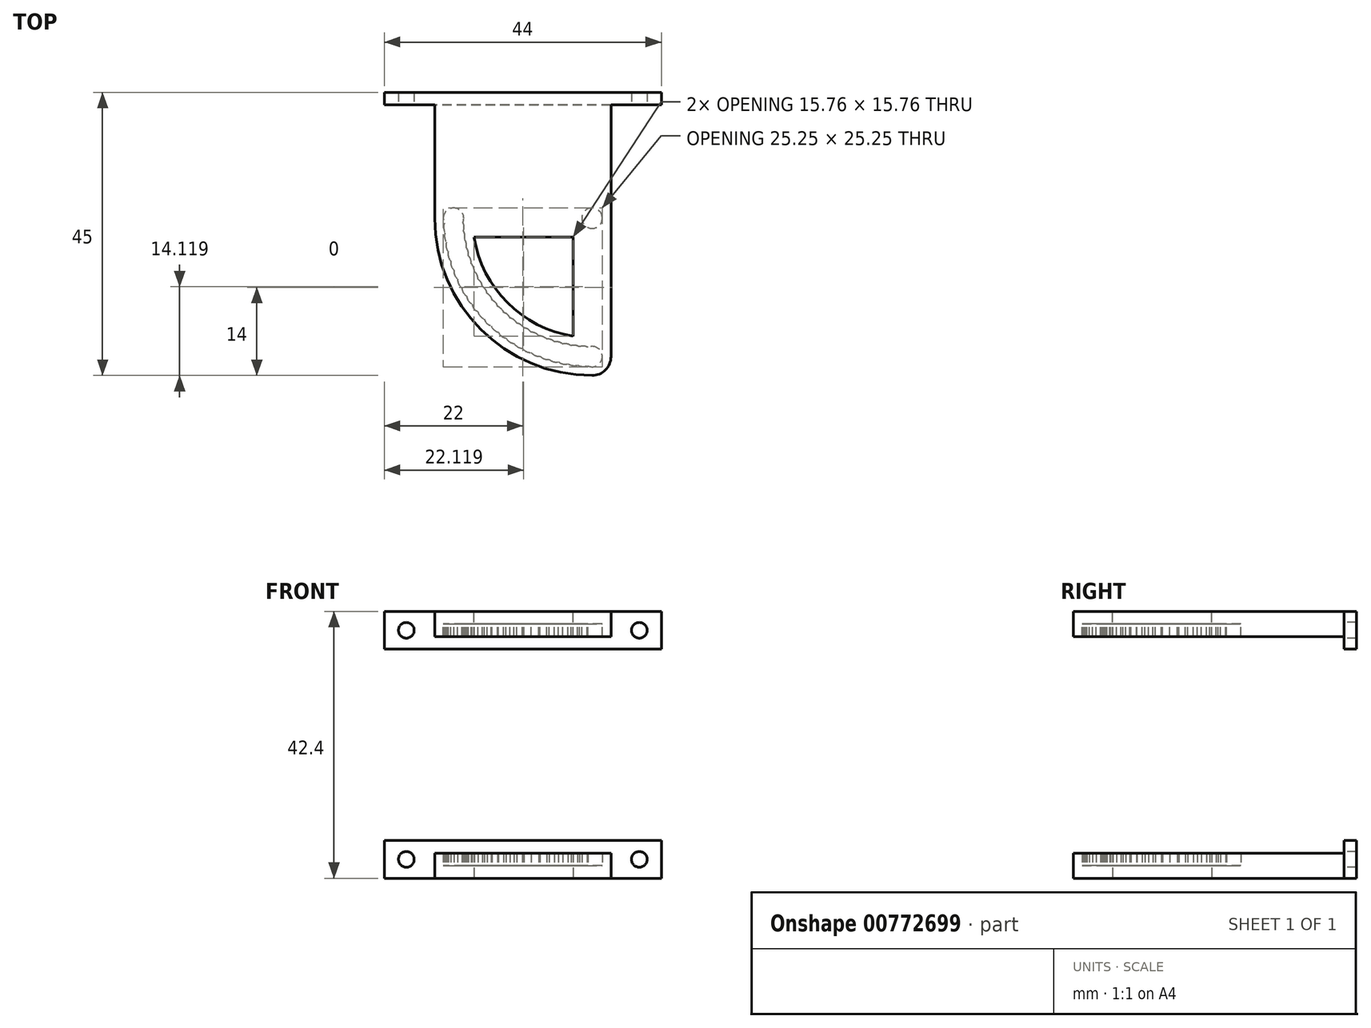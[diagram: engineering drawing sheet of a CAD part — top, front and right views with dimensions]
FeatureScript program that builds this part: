
annotation { "Feature Type Name" : "Feature", "Feature Type Description" : "" }
export const myFeature = defineFeature(function(context is Context, id is Id, definition is map)
    precondition{}
    {
        {
            var Q0;
            Q0=qCreatedBy(makeId("Top.planeOp"),FACE);
            var sketch = newSketch(context, id + "F0", { "sketchPlane" : qUnion([Q0])});
            skArc(sketch, "E0", {"start": v(-25, 0) * mm, "mid": v(-17.68, -17.68) * mm, "end": v(0, -25) * mm});
            skCircle(sketch, "E1", {"center": v(0, 0) * mm, "radius": 1.63 * mm});
            skArc(sketch, "E2", {"start": v(-0.77, -23.43) * mm, "mid": v(1.62, -22.05) * mm, "end": v(-0.67, -20.52) * mm});
            skCircle(sketch, "E3", {"center": v(0, 0) * mm, "radius": 22 * mm, "construction": true});
            skArc(sketch, "E4", {"start": v(-18.76, -3) * mm, "mid": v(-13.44, -13.44) * mm, "end": v(-3, -18.76) * mm});
            skLineSegment(sketch, "E5", {"start": v(3, -22) * mm, "end": v(3, 20) * mm});
            skLineSegment(sketch, "E6", {"start": v(3, 20) * mm, "end": v(-25, 20) * mm});
            skLineSegment(sketch, "E7", {"start": v(-5.92, -22) * mm, "end": v(6.06, -22) * mm, "construction": true});
            skLineSegment(sketch, "E8", {"start": v(-28.17, 0) * mm, "end": v(-21.36, 0) * mm, "construction": true});
            skLineSegment(sketch, "E9", {"start": v(-25, 0) * mm, "end": v(-25, 20) * mm});
            skLineSegment(sketch, "E10", {"start": v(-3, -18.76) * mm, "end": v(-3, -3) * mm});
            skLineSegment(sketch, "E11", {"start": v(-3, -3) * mm, "end": v(-18.76, -3) * mm});
            skArc(sketch, "E12.1.0", {"start": v(-2.3, -23.33) * mm, "mid": v(-1.55, -23.57) * mm, "end": v(-0.77, -23.43) * mm});
            skArc(sketch, "E12.2.0", {"start": v(-3.82, -23.13) * mm, "mid": v(-3.08, -23.42) * mm, "end": v(-2.3, -23.33) * mm});
            skArc(sketch, "E12.3.0", {"start": v(-5.88, -21.93) * mm, "mid": v(-5.87, -21.97) * mm, "end": v(-5.86, -22) * mm});
            skArc(sketch, "E12.4.0", {"start": v(-6.8, -22.44) * mm, "mid": v(-6.11, -22.82) * mm, "end": v(-5.32, -22.83) * mm});
            skArc(sketch, "E12.5.0", {"start": v(-8.26, -21.94) * mm, "mid": v(-7.6, -22.37) * mm, "end": v(-6.8, -22.44) * mm});
            skArc(sketch, "E12.6.0", {"start": v(-9.68, -21.36) * mm, "mid": v(-9.04, -21.83) * mm, "end": v(-8.26, -21.94) * mm});
            skArc(sketch, "E12.7.0", {"start": v(-11.05, -20.68) * mm, "mid": v(-10.45, -21.19) * mm, "end": v(-9.68, -21.36) * mm});
            skArc(sketch, "E12.8.0", {"start": v(-12.38, -19.9) * mm, "mid": v(-11.81, -20.46) * mm, "end": v(-11.05, -20.68) * mm});
            skArc(sketch, "E12.9.0", {"start": v(-13.66, -19.06) * mm, "mid": v(-13.13, -19.64) * mm, "end": v(-12.38, -19.9) * mm});
            skArc(sketch, "E12.10.0", {"start": v(-14.87, -18.12) * mm, "mid": v(-14.38, -18.74) * mm, "end": v(-13.66, -19.06) * mm});
            skArc(sketch, "E12.11.0", {"start": v(-16.03, -17.11) * mm, "mid": v(-15.58, -17.76) * mm, "end": v(-14.87, -18.12) * mm});
            skArc(sketch, "E12.12.0", {"start": v(-17.11, -16.03) * mm, "mid": v(-16.7, -16.7) * mm, "end": v(-16.03, -17.11) * mm});
            skArc(sketch, "E12.13.0", {"start": v(-18.12, -14.87) * mm, "mid": v(-17.76, -15.58) * mm, "end": v(-17.11, -16.03) * mm});
            skArc(sketch, "E12.14.0", {"start": v(-19.06, -13.66) * mm, "mid": v(-18.74, -14.38) * mm, "end": v(-18.12, -14.87) * mm});
            skArc(sketch, "E12.15.0", {"start": v(-19.9, -12.38) * mm, "mid": v(-19.64, -13.13) * mm, "end": v(-19.06, -13.66) * mm});
            skArc(sketch, "E12.16.0", {"start": v(-20.68, -11.05) * mm, "mid": v(-20.46, -11.81) * mm, "end": v(-19.9, -12.38) * mm});
            skArc(sketch, "E12.17.0", {"start": v(-21.36, -9.68) * mm, "mid": v(-21.19, -10.45) * mm, "end": v(-20.68, -11.05) * mm});
            skArc(sketch, "E12.18.0", {"start": v(-21.94, -8.26) * mm, "mid": v(-21.83, -9.04) * mm, "end": v(-21.36, -9.68) * mm});
            skArc(sketch, "E12.19.0", {"start": v(-22.44, -6.8) * mm, "mid": v(-22.37, -7.6) * mm, "end": v(-21.94, -8.26) * mm});
            skLineSegment(sketch, "E12.anchor1", {"start": v(0, 0) * mm, "end": v(0, -22) * mm, "construction": true});
            skLineSegment(sketch, "E12.anchor2", {"start": v(0, 0) * mm, "end": v(-22, 0) * mm, "construction": true});
            skArc(sketch, "E13.1.20.0", {"start": v(-22.83, -5.32) * mm, "mid": v(-22.82, -6.11) * mm, "end": v(-22.44, -6.8) * mm});
            skArc(sketch, "E13.1.21.0", {"start": v(-23.13, -3.82) * mm, "mid": v(-23.17, -4.6) * mm, "end": v(-22.83, -5.32) * mm});
            skArc(sketch, "E13.1.22.0", {"start": v(-23.33, -2.3) * mm, "mid": v(-23.42, -3.08) * mm, "end": v(-23.13, -3.82) * mm});
            skArc(sketch, "E13.1.23.0", {"start": v(-23.43, -0.77) * mm, "mid": v(-23.57, -1.55) * mm, "end": v(-23.33, -2.3) * mm});
            skArc(sketch, "E13.1.24.0", {"start": v(-20.52, -0.67) * mm, "mid": v(-22.05, 1.62) * mm, "end": v(-23.43, -0.77) * mm});
            skArc(sketch, "E14.trimOffspring", {"start": v(-20.26, -3.34) * mm, "mid": v(-20.2, -2.66) * mm, "end": v(-20.43, -2.01) * mm});
            skArc(sketch, "E15.trimOffspring", {"start": v(-20.43, -2.01) * mm, "mid": v(-20.33, -1.33) * mm, "end": v(-20.52, -0.67) * mm});
            skArc(sketch, "E16.trimOffspring", {"start": v(-20, -4.66) * mm, "mid": v(-19.98, -3.97) * mm, "end": v(-20.26, -3.34) * mm});
            skArc(sketch, "E17.trimOffspring", {"start": v(-19.65, -5.96) * mm, "mid": v(-19.68, -5.27) * mm, "end": v(-20, -4.66) * mm});
            skArc(sketch, "E18.trimOffspring", {"start": v(-19.22, -7.23) * mm, "mid": v(-19.3, -6.55) * mm, "end": v(-19.65, -5.96) * mm});
            skArc(sketch, "E19.trimOffspring", {"start": v(-18.7, -8.47) * mm, "mid": v(-18.82, -7.8) * mm, "end": v(-19.22, -7.23) * mm});
            skArc(sketch, "E20.trimOffspring", {"start": v(-18.1, -9.68) * mm, "mid": v(-18.27, -9.01) * mm, "end": v(-18.7, -8.47) * mm});
            skArc(sketch, "E21.trimOffspring", {"start": v(-17.44, -10.84) * mm, "mid": v(-17.65, -10.19) * mm, "end": v(-18.1, -9.68) * mm});
            skArc(sketch, "E22.trimOffspring", {"start": v(-16.69, -11.96) * mm, "mid": v(-16.94, -11.32) * mm, "end": v(-17.44, -10.84) * mm});
            skArc(sketch, "E23.trimOffspring", {"start": v(-15.87, -13.02) * mm, "mid": v(-16.16, -12.4) * mm, "end": v(-16.69, -11.96) * mm});
            skArc(sketch, "E24.trimOffspring", {"start": v(-14.99, -14.04) * mm, "mid": v(-15.32, -13.43) * mm, "end": v(-15.87, -13.02) * mm});
            skArc(sketch, "E25.trimOffspring", {"start": v(-14.04, -14.99) * mm, "mid": v(-14.4, -14.4) * mm, "end": v(-14.99, -14.04) * mm});
            skArc(sketch, "E26.trimOffspring", {"start": v(-13.02, -15.87) * mm, "mid": v(-13.43, -15.32) * mm, "end": v(-14.04, -14.99) * mm});
            skArc(sketch, "E27.trimOffspring", {"start": v(-11.96, -16.69) * mm, "mid": v(-12.4, -16.16) * mm, "end": v(-13.02, -15.87) * mm});
            skArc(sketch, "E28.trimOffspring", {"start": v(-10.84, -17.44) * mm, "mid": v(-11.32, -16.94) * mm, "end": v(-11.96, -16.69) * mm});
            skArc(sketch, "E29.trimOffspring", {"start": v(-9.68, -18.1) * mm, "mid": v(-10.19, -17.65) * mm, "end": v(-10.84, -17.44) * mm});
            skArc(sketch, "E30.trimOffspring", {"start": v(-8.47, -18.7) * mm, "mid": v(-9.01, -18.27) * mm, "end": v(-9.68, -18.1) * mm});
            skArc(sketch, "E31.trimOffspring", {"start": v(-7.23, -19.22) * mm, "mid": v(-7.8, -18.82) * mm, "end": v(-8.47, -18.7) * mm});
            skArc(sketch, "E32.trimOffspring", {"start": v(-5.96, -19.65) * mm, "mid": v(-6.55, -19.3) * mm, "end": v(-7.23, -19.22) * mm});
            skArc(sketch, "E33.trimOffspring", {"start": v(-5.32, -22.83) * mm, "mid": v(-4.6, -23.17) * mm, "end": v(-3.82, -23.13) * mm});
            skArc(sketch, "E34.trimOffspring", {"start": v(-4.66, -20) * mm, "mid": v(-5.27, -19.68) * mm, "end": v(-5.96, -19.65) * mm});
            skArc(sketch, "E35.trimOffspring", {"start": v(-3.34, -20.26) * mm, "mid": v(-3.97, -19.98) * mm, "end": v(-4.66, -20) * mm});
            skArc(sketch, "E36.trimOffspring", {"start": v(-2.01, -20.43) * mm, "mid": v(-2.66, -20.2) * mm, "end": v(-3.34, -20.26) * mm});
            skArc(sketch, "E37.trimOffspring", {"start": v(-1.26, -22) * mm, "mid": v(-1.26, -21.98) * mm, "end": v(-1.25, -21.96) * mm});
            skArc(sketch, "E38.trimOffspring", {"start": v(-0.67, -20.52) * mm, "mid": v(-1.33, -20.33) * mm, "end": v(-2.01, -20.43) * mm});
            skArc(sketch, "E39", {"start": v(0, -25) * mm, "mid": v(2.12, -24.12) * mm, "end": v(3, -22) * mm});
            skSolve(sketch);
        }
        {
            var Q0;
            Q0=makeQuery(id+"F0.imprint","IMPRINT",FACE,{"disambiguationData":[TD([[makeQuery(id+"F0.imprint","IMPRINT",EDGE,{"derivedFrom":sQuery(id+"F0.wireOp",EDGE,"E0")}),1.0]])]});
            extrude(context, id + "F1", {"entities" : qUnion([Q0]), "depth" : 2 * mm, "offsetDistance" : 25 * mm});
        }
        {
            var Q0;
            Q0=makeQuery(id+"F1.opExtrude","CAP_FACE",FACE,{"disambiguationData":[OSD([sQuery(id+"F0.wireOp",EDGE,"E0"),sQuery(id+"F0.wireOp",EDGE,"E1"),sQuery(id+"F0.wireOp",EDGE,"E2"),sQuery(id+"F0.wireOp",EDGE,"E4"),sQuery(id+"F0.wireOp",EDGE,"E5"),sQuery(id+"F0.wireOp",EDGE,"E6"),sQuery(id+"F0.wireOp",EDGE,"E9"),sQuery(id+"F0.wireOp",EDGE,"E10"),sQuery(id+"F0.wireOp",EDGE,"E11"),sQuery(id+"F0.wireOp",EDGE,"E12.1.0"),sQuery(id+"F0.wireOp",EDGE,"E12.2.0"),sQuery(id+"F0.wireOp",EDGE,"E12.4.0"),sQuery(id+"F0.wireOp",EDGE,"E12.5.0"),sQuery(id+"F0.wireOp",EDGE,"E12.6.0"),sQuery(id+"F0.wireOp",EDGE,"E12.7.0"),sQuery(id+"F0.wireOp",EDGE,"E12.8.0"),sQuery(id+"F0.wireOp",EDGE,"E12.9.0"),sQuery(id+"F0.wireOp",EDGE,"E12.10.0"),sQuery(id+"F0.wireOp",EDGE,"E12.11.0"),sQuery(id+"F0.wireOp",EDGE,"E12.12.0"),sQuery(id+"F0.wireOp",EDGE,"E12.13.0"),sQuery(id+"F0.wireOp",EDGE,"E12.14.0"),sQuery(id+"F0.wireOp",EDGE,"E12.15.0"),sQuery(id+"F0.wireOp",EDGE,"E12.16.0"),sQuery(id+"F0.wireOp",EDGE,"E12.17.0"),sQuery(id+"F0.wireOp",EDGE,"E12.18.0"),sQuery(id+"F0.wireOp",EDGE,"E12.19.0"),sQuery(id+"F0.wireOp",EDGE,"E13.1.20.0"),sQuery(id+"F0.wireOp",EDGE,"E13.1.21.0"),sQuery(id+"F0.wireOp",EDGE,"E13.1.22.0"),sQuery(id+"F0.wireOp",EDGE,"E13.1.23.0"),sQuery(id+"F0.wireOp",EDGE,"E13.1.24.0"),sQuery(id+"F0.wireOp",EDGE,"E14.trimOffspring"),sQuery(id+"F0.wireOp",EDGE,"E15.trimOffspring"),sQuery(id+"F0.wireOp",EDGE,"E16.trimOffspring"),sQuery(id+"F0.wireOp",EDGE,"E17.trimOffspring"),sQuery(id+"F0.wireOp",EDGE,"E18.trimOffspring"),sQuery(id+"F0.wireOp",EDGE,"E19.trimOffspring"),sQuery(id+"F0.wireOp",EDGE,"E20.trimOffspring"),sQuery(id+"F0.wireOp",EDGE,"E21.trimOffspring"),sQuery(id+"F0.wireOp",EDGE,"E22.trimOffspring"),sQuery(id+"F0.wireOp",EDGE,"E23.trimOffspring"),sQuery(id+"F0.wireOp",EDGE,"E24.trimOffspring"),sQuery(id+"F0.wireOp",EDGE,"E25.trimOffspring"),sQuery(id+"F0.wireOp",EDGE,"E26.trimOffspring"),sQuery(id+"F0.wireOp",EDGE,"E27.trimOffspring"),sQuery(id+"F0.wireOp",EDGE,"E28.trimOffspring"),sQuery(id+"F0.wireOp",EDGE,"E29.trimOffspring"),sQuery(id+"F0.wireOp",EDGE,"E30.trimOffspring"),sQuery(id+"F0.wireOp",EDGE,"E31.trimOffspring"),sQuery(id+"F0.wireOp",EDGE,"E32.trimOffspring"),sQuery(id+"F0.wireOp",EDGE,"E33.trimOffspring"),sQuery(id+"F0.wireOp",EDGE,"E34.trimOffspring"),sQuery(id+"F0.wireOp",EDGE,"E35.trimOffspring"),sQuery(id+"F0.wireOp",EDGE,"E36.trimOffspring"),sQuery(id+"F0.wireOp",EDGE,"E38.trimOffspring"),sQuery(id+"F0.wireOp",EDGE,"E39")])],"isStart":true});
            var sketch = newSketch(context, id + "F2", { "sketchPlane" : qUnion([Q0])});
            skArc(sketch, "E40.0", {"start": v(-25, 0) * mm, "mid": v(-17.68, 17.68) * mm, "end": v(0, 25) * mm});
            skPoint(sketch, "E41.0", {"position": v(2.12, 24.12) * mm});
            skLineSegment(sketch, "E42.0", {"start": v(3, 22) * mm, "end": v(3, -20) * mm});
            skLineSegment(sketch, "E43.0", {"start": v(-25, 0) * mm, "end": v(-25, -20) * mm});
            skLineSegment(sketch, "E44.0", {"start": v(3, -20) * mm, "end": v(-25, -20) * mm});
            skLineSegment(sketch, "E45.0", {"start": v(-3, 3) * mm, "end": v(-18.76, 3) * mm});
            skArc(sketch, "E46.0", {"start": v(-18.76, 3) * mm, "mid": v(-13.44, 13.44) * mm, "end": v(-3, 18.76) * mm});
            skPoint(sketch, "E47.0", {"position": v(-3, 10.88) * mm});
            skLineSegment(sketch, "E48.0", {"start": v(-3, 18.76) * mm, "end": v(-3, 3) * mm});
            skSolve(sketch);
        }
        {
            var Q0;
            Q0=makeQuery(id+"F2.imprint","IMPRINT",FACE,{"disambiguationData":[TD([[makeQuery(id+"F2.imprint","IMPRINT",EDGE,{"derivedFrom":sQuery(id+"F2.wireOp",EDGE,"E40.0")}),-1.0]])]});
            var Q1;
            Q1=makeQuery(id+"F2.imprint","IMPRINT",FACE,{"disambiguationData":[TD([[makeQuery(id+"F2.imprint","IMPRINT",EDGE,{"derivedFrom":makeQuery(id+"F1.opExtrude","CAP_EDGE",EDGE,{"disambiguationData":[OSD([sQuery(id+"F0.wireOp",EDGE,"E2")])],"isStart":true})}),-1.0]])]});
            var Q2;
            Q2=makeQuery(id+"F2.imprint","IMPRINT",FACE,{"disambiguationData":[TD([[makeQuery(id+"F2.imprint","IMPRINT",EDGE,{"derivedFrom":makeQuery(id+"F1.opExtrude","CAP_EDGE",EDGE,{"disambiguationData":[OSD([sQuery(id+"F0.wireOp",EDGE,"E1")])],"isStart":true})}),-1.0]])]});
            extrude(context, id + "F3", {"entities" : qUnion([Q0, Q1, Q2]), "operationType" : NewBodyOperationType.ADD, "depth" : 2 * mm, "offsetDistance" : 25 * mm});
        }
        {
            var Q0;
            Q0=makeQuery(id+"F1.opExtrude","CAP_FACE",FACE,{"disambiguationData":[OSD([sQuery(id+"F0.wireOp",EDGE,"E0"),sQuery(id+"F0.wireOp",EDGE,"E1"),sQuery(id+"F0.wireOp",EDGE,"E2"),sQuery(id+"F0.wireOp",EDGE,"E4"),sQuery(id+"F0.wireOp",EDGE,"E5"),sQuery(id+"F0.wireOp",EDGE,"E6"),sQuery(id+"F0.wireOp",EDGE,"E9"),sQuery(id+"F0.wireOp",EDGE,"E10"),sQuery(id+"F0.wireOp",EDGE,"E11"),sQuery(id+"F0.wireOp",EDGE,"E12.1.0"),sQuery(id+"F0.wireOp",EDGE,"E12.2.0"),sQuery(id+"F0.wireOp",EDGE,"E12.4.0"),sQuery(id+"F0.wireOp",EDGE,"E12.5.0"),sQuery(id+"F0.wireOp",EDGE,"E12.6.0"),sQuery(id+"F0.wireOp",EDGE,"E12.7.0"),sQuery(id+"F0.wireOp",EDGE,"E12.8.0"),sQuery(id+"F0.wireOp",EDGE,"E12.9.0"),sQuery(id+"F0.wireOp",EDGE,"E12.10.0"),sQuery(id+"F0.wireOp",EDGE,"E12.11.0"),sQuery(id+"F0.wireOp",EDGE,"E12.12.0"),sQuery(id+"F0.wireOp",EDGE,"E12.13.0"),sQuery(id+"F0.wireOp",EDGE,"E12.14.0"),sQuery(id+"F0.wireOp",EDGE,"E12.15.0"),sQuery(id+"F0.wireOp",EDGE,"E12.16.0"),sQuery(id+"F0.wireOp",EDGE,"E12.17.0"),sQuery(id+"F0.wireOp",EDGE,"E12.18.0"),sQuery(id+"F0.wireOp",EDGE,"E12.19.0"),sQuery(id+"F0.wireOp",EDGE,"E13.1.20.0"),sQuery(id+"F0.wireOp",EDGE,"E13.1.21.0"),sQuery(id+"F0.wireOp",EDGE,"E13.1.22.0"),sQuery(id+"F0.wireOp",EDGE,"E13.1.23.0"),sQuery(id+"F0.wireOp",EDGE,"E13.1.24.0"),sQuery(id+"F0.wireOp",EDGE,"E14.trimOffspring"),sQuery(id+"F0.wireOp",EDGE,"E15.trimOffspring"),sQuery(id+"F0.wireOp",EDGE,"E16.trimOffspring"),sQuery(id+"F0.wireOp",EDGE,"E17.trimOffspring"),sQuery(id+"F0.wireOp",EDGE,"E18.trimOffspring"),sQuery(id+"F0.wireOp",EDGE,"E19.trimOffspring"),sQuery(id+"F0.wireOp",EDGE,"E20.trimOffspring"),sQuery(id+"F0.wireOp",EDGE,"E21.trimOffspring"),sQuery(id+"F0.wireOp",EDGE,"E22.trimOffspring"),sQuery(id+"F0.wireOp",EDGE,"E23.trimOffspring"),sQuery(id+"F0.wireOp",EDGE,"E24.trimOffspring"),sQuery(id+"F0.wireOp",EDGE,"E25.trimOffspring"),sQuery(id+"F0.wireOp",EDGE,"E26.trimOffspring"),sQuery(id+"F0.wireOp",EDGE,"E27.trimOffspring"),sQuery(id+"F0.wireOp",EDGE,"E28.trimOffspring"),sQuery(id+"F0.wireOp",EDGE,"E29.trimOffspring"),sQuery(id+"F0.wireOp",EDGE,"E30.trimOffspring"),sQuery(id+"F0.wireOp",EDGE,"E31.trimOffspring"),sQuery(id+"F0.wireOp",EDGE,"E32.trimOffspring"),sQuery(id+"F0.wireOp",EDGE,"E33.trimOffspring"),sQuery(id+"F0.wireOp",EDGE,"E34.trimOffspring"),sQuery(id+"F0.wireOp",EDGE,"E35.trimOffspring"),sQuery(id+"F0.wireOp",EDGE,"E36.trimOffspring"),sQuery(id+"F0.wireOp",EDGE,"E38.trimOffspring"),sQuery(id+"F0.wireOp",EDGE,"E39")])],"isStart":false});
            var sketch = newSketch(context, id + "F4", { "sketchPlane" : qUnion([Q0])});
            skLineSegment(sketch, "E49.bottom", {"start": v(-33, 20) * mm, "end": v(11, 20) * mm});
            skLineSegment(sketch, "E49.top", {"start": v(-33, 18) * mm, "end": v(11, 18) * mm});
            skLineSegment(sketch, "E49.left", {"start": v(-33, 20) * mm, "end": v(-33, 18) * mm});
            skLineSegment(sketch, "E49.right", {"start": v(11, 20) * mm, "end": v(11, 18) * mm});
            skLineSegment(sketch, "E50", {"start": v(-11, 37.96) * mm, "end": v(-11, -28.64) * mm, "construction": true});
            skSolve(sketch);
        }
        {
            var Q0;
            {var subQ3=sQuery(id+"F4.wireOp",EDGE,"E49.left");Q0=makeQuery(id+"F4.imprint","IMPRINT",FACE,{"disambiguationData":[TD([[makeQuery(id+"F4.imprint","IMPRINT",EDGE,{"derivedFrom":subQ3}),1.0]])]});}
            var Q1;
            {var subQ0=sQuery(id+"F4.wireOp",EDGE,"E49.bottom");var subQ1=makeQuery(id+"F1.opExtrude","CAP_EDGE",EDGE,{"disambiguationData":[OSD([sQuery(id+"F0.wireOp",EDGE,"E5")])],"isStart":false});var subQ2=makeQuery(id+"F4.imprint","INTERSECT",VERTEX,{"derivedFrom":[subQ1,subQ0]});var subQ3=makeQuery(id+"F1.opExtrude","CAP_EDGE",EDGE,{"disambiguationData":[OSD([sQuery(id+"F0.wireOp",EDGE,"E9")])],"isStart":false});var subQ4=makeQuery(id+"F4.imprint","INTERSECT",VERTEX,{"derivedFrom":[subQ3,subQ0]});Q1=makeQuery(id+"F4.imprint","IMPRINT",FACE,{"disambiguationData":[TD([[makeQuery(id+"F4.imprint","IMPRINT",EDGE,{"disambiguationData":[TD([[subQ2,-1.0],[subQ4,1.0]])],"derivedFrom":subQ0}),1.0]])]});}
            var Q2;
            {var subQ3=sQuery(id+"F4.wireOp",EDGE,"E49.right");Q2=makeQuery(id+"F4.imprint","IMPRINT",FACE,{"disambiguationData":[TD([[makeQuery(id+"F4.imprint","IMPRINT",EDGE,{"derivedFrom":subQ3}),-1.0]])]});}
            extrude(context, id + "F5", {"entities" : qUnion([Q0, Q1, Q2]), "operationType" : NewBodyOperationType.ADD, "depth" : 2 * mm, "offsetDistance" : 25 * mm, "hasSecondDirection" : true, "secondDirectionOppositeDirection" : true, "secondDirectionDepth" : 4 * mm});
        }
        {
            var Q0;
            Q0=makeQuery(id+"F5.opExtrude","SWEPT_FACE",FACE,{"disambiguationData":[OSD([sQuery(id+"F4.wireOp",EDGE,"E49.top")])]});
            var sketch = newSketch(context, id + "F6", { "sketchPlane" : qUnion([Q0])});
            skCircle(sketch, "E51", {"center": v(-29.5, 1) * mm, "radius": 1.25 * mm});
            skLineSegment(sketch, "E52", {"start": v(-34.85, 1) * mm, "end": v(16.96, 1) * mm, "construction": true});
            skCircle(sketch, "E53", {"center": v(7.5, 1) * mm, "radius": 1.25 * mm});
            skSolve(sketch);
        }
        {
            var Q0;
            Q0=makeQuery(id+"F6.imprint","IMPRINT",FACE,{"disambiguationData":[TD([[makeQuery(id+"F6.imprint","IMPRINT",EDGE,{"derivedFrom":sQuery(id+"F6.wireOp",EDGE,"E53")}),1.0]])]});
            var Q1;
            Q1=makeQuery(id+"F6.imprint","IMPRINT",FACE,{"disambiguationData":[TD([[makeQuery(id+"F6.imprint","IMPRINT",EDGE,{"derivedFrom":sQuery(id+"F6.wireOp",EDGE,"E51")}),1.0]])]});
            extrude(context, id + "F7", {"entities" : qUnion([Q0, Q1]), "operationType" : NewBodyOperationType.REMOVE, "oppositeDirection" : true, "depth" : 25 * mm, "offsetDistance" : 25 * mm});
        }
        {
            var Q0;
            Q0=qCreatedBy(makeId("Top.planeOp"),FACE);
            cPlane(context, id + "F8", {"entities" : qUnion([Q0]), "cplaneType" : CPlaneType.OFFSET, "offset" : 19.2 * mm, "width" : 150 * mm, "height" : 150 * mm});
        }
        {
            var Q0;
            Q0=makeQuery(id+"F1.opExtrude","SWEPT_BODY",BODY,{"disambiguationData":[OSD([sQuery(id+"F0.wireOp",EDGE,"E0"),sQuery(id+"F0.wireOp",EDGE,"E1"),sQuery(id+"F0.wireOp",EDGE,"E2"),sQuery(id+"F0.wireOp",EDGE,"E4"),sQuery(id+"F0.wireOp",EDGE,"E5"),sQuery(id+"F0.wireOp",EDGE,"E6"),sQuery(id+"F0.wireOp",EDGE,"E9"),sQuery(id+"F0.wireOp",EDGE,"E10"),sQuery(id+"F0.wireOp",EDGE,"E11"),sQuery(id+"F0.wireOp",EDGE,"E12.1.0"),sQuery(id+"F0.wireOp",EDGE,"E12.2.0"),sQuery(id+"F0.wireOp",EDGE,"E12.4.0"),sQuery(id+"F0.wireOp",EDGE,"E12.5.0"),sQuery(id+"F0.wireOp",EDGE,"E12.6.0"),sQuery(id+"F0.wireOp",EDGE,"E12.7.0"),sQuery(id+"F0.wireOp",EDGE,"E12.8.0"),sQuery(id+"F0.wireOp",EDGE,"E12.9.0"),sQuery(id+"F0.wireOp",EDGE,"E12.10.0"),sQuery(id+"F0.wireOp",EDGE,"E12.11.0"),sQuery(id+"F0.wireOp",EDGE,"E12.12.0"),sQuery(id+"F0.wireOp",EDGE,"E12.13.0"),sQuery(id+"F0.wireOp",EDGE,"E12.14.0"),sQuery(id+"F0.wireOp",EDGE,"E12.15.0"),sQuery(id+"F0.wireOp",EDGE,"E12.16.0"),sQuery(id+"F0.wireOp",EDGE,"E12.17.0"),sQuery(id+"F0.wireOp",EDGE,"E12.18.0"),sQuery(id+"F0.wireOp",EDGE,"E12.19.0"),sQuery(id+"F0.wireOp",EDGE,"E13.1.20.0"),sQuery(id+"F0.wireOp",EDGE,"E13.1.21.0"),sQuery(id+"F0.wireOp",EDGE,"E13.1.22.0"),sQuery(id+"F0.wireOp",EDGE,"E13.1.23.0"),sQuery(id+"F0.wireOp",EDGE,"E13.1.24.0"),sQuery(id+"F0.wireOp",EDGE,"E14.trimOffspring"),sQuery(id+"F0.wireOp",EDGE,"E15.trimOffspring"),sQuery(id+"F0.wireOp",EDGE,"E16.trimOffspring"),sQuery(id+"F0.wireOp",EDGE,"E17.trimOffspring"),sQuery(id+"F0.wireOp",EDGE,"E18.trimOffspring"),sQuery(id+"F0.wireOp",EDGE,"E19.trimOffspring"),sQuery(id+"F0.wireOp",EDGE,"E20.trimOffspring"),sQuery(id+"F0.wireOp",EDGE,"E21.trimOffspring"),sQuery(id+"F0.wireOp",EDGE,"E22.trimOffspring"),sQuery(id+"F0.wireOp",EDGE,"E23.trimOffspring"),sQuery(id+"F0.wireOp",EDGE,"E24.trimOffspring"),sQuery(id+"F0.wireOp",EDGE,"E25.trimOffspring"),sQuery(id+"F0.wireOp",EDGE,"E26.trimOffspring"),sQuery(id+"F0.wireOp",EDGE,"E27.trimOffspring"),sQuery(id+"F0.wireOp",EDGE,"E28.trimOffspring"),sQuery(id+"F0.wireOp",EDGE,"E29.trimOffspring"),sQuery(id+"F0.wireOp",EDGE,"E30.trimOffspring"),sQuery(id+"F0.wireOp",EDGE,"E31.trimOffspring"),sQuery(id+"F0.wireOp",EDGE,"E32.trimOffspring"),sQuery(id+"F0.wireOp",EDGE,"E33.trimOffspring"),sQuery(id+"F0.wireOp",EDGE,"E34.trimOffspring"),sQuery(id+"F0.wireOp",EDGE,"E35.trimOffspring"),sQuery(id+"F0.wireOp",EDGE,"E36.trimOffspring"),sQuery(id+"F0.wireOp",EDGE,"E38.trimOffspring"),sQuery(id+"F0.wireOp",EDGE,"E39")])]});
            var Q1;
            Q1=qCreatedBy(id+"F8.planeOp",FACE);
            mirror(context, id + "F9", {"entities" : qUnion([Q0]), "mirrorPlane" : qUnion([Q1])});
        }
    });
